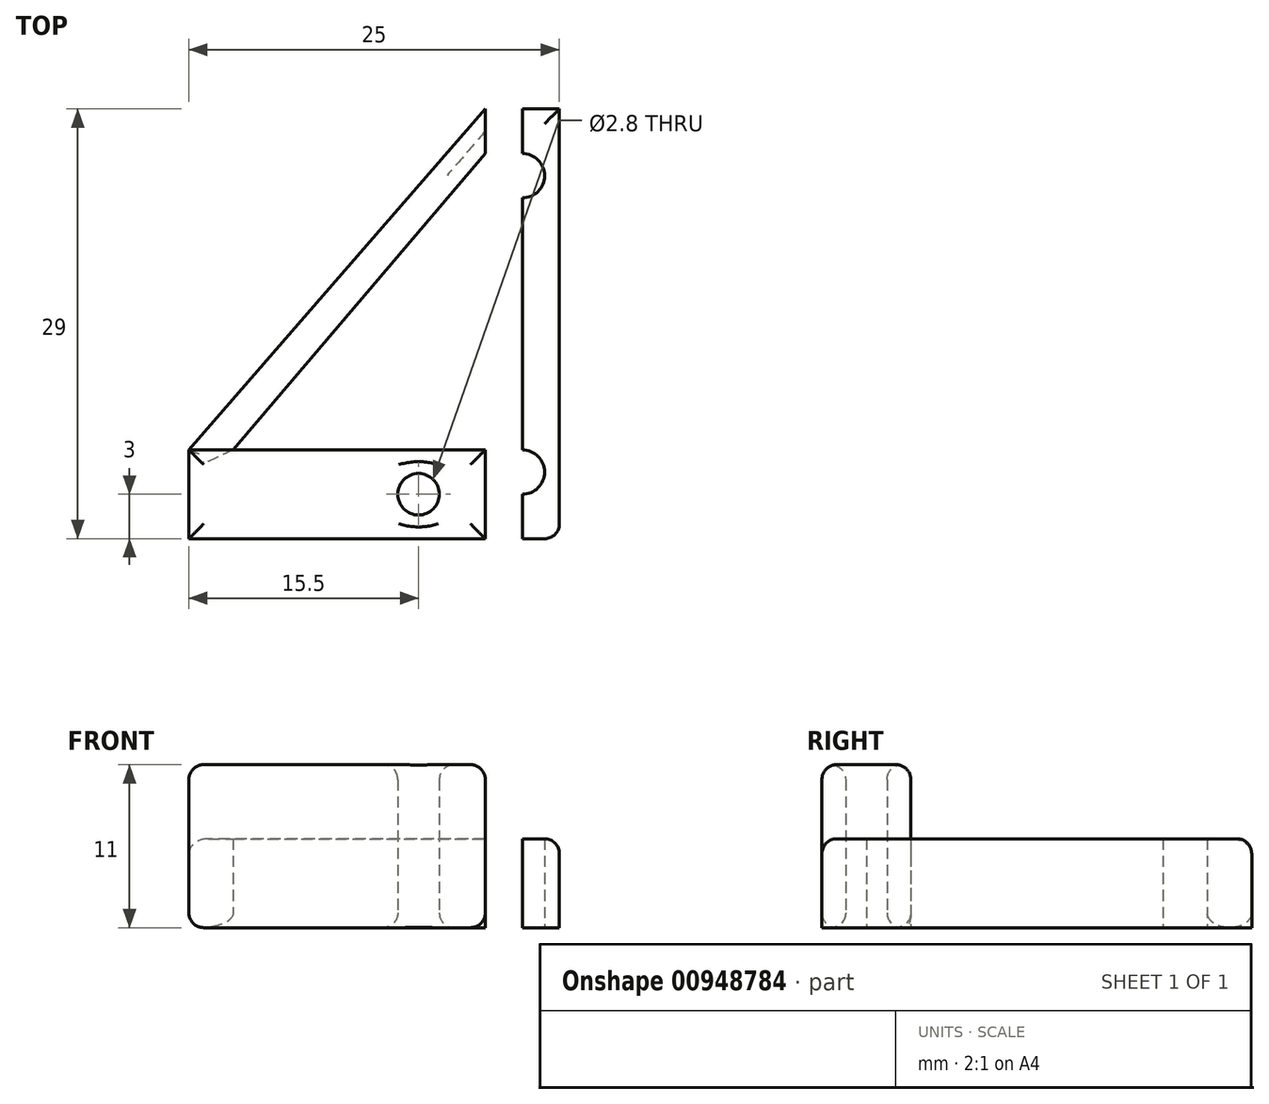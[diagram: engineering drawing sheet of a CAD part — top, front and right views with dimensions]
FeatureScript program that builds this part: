
annotation { "Feature Type Name" : "Feature", "Feature Type Description" : "" }
export const myFeature = defineFeature(function(context is Context, id is Id, definition is map)
    precondition{}
    {
        {
            var Q0;
            Q0=qCreatedBy(makeId("Top.planeOp"),FACE);
            var sketch = newSketch(context, id + "F0", { "sketchPlane" : qUnion([Q0])});
            skLineSegment(sketch, "E0.bottom", {"start": v(0, 0) * mm, "end": v(-20, 0) * mm});
            skLineSegment(sketch, "E0.top", {"start": v(0, 6) * mm, "end": v(-20, 6) * mm});
            skLineSegment(sketch, "E0.left", {"start": v(0, 0) * mm, "end": v(0, 6) * mm});
            skLineSegment(sketch, "E0.right", {"start": v(-20, 0) * mm, "end": v(-20, 6) * mm});
            skLineSegment(sketch, "E1", {"start": v(-20, 3) * mm, "end": v(0, 3) * mm});
            skCircle(sketch, "E2", {"center": v(-15.5, 3) * mm, "radius": 1.4 * mm});
            skCircle(sketch, "E3", {"center": v(-4.5, 3) * mm, "radius": 1.4 * mm});
            skPoint(sketch, "E4", {"position": v(-15.5, 4.4) * mm});
            skPoint(sketch, "E5", {"position": v(-4.5, 4.4) * mm});
            skPoint(sketch, "E6", {"position": v(-4.5, 1.6) * mm});
            skPoint(sketch, "E7", {"position": v(-15.5, 1.6) * mm});
            skLineSegment(sketch, "E8", {"start": v(-15.5, 4.4) * mm, "end": v(-4.5, 4.4) * mm});
            skLineSegment(sketch, "E9", {"start": v(-4.5, 1.6) * mm, "end": v(-15.5, 1.6) * mm});
            skLineSegment(sketch, "E10.bottom", {"start": v(0, 0) * mm, "end": v(5, 0) * mm});
            skLineSegment(sketch, "E10.top", {"start": v(0, 29) * mm, "end": v(5, 29) * mm});
            skLineSegment(sketch, "E10.left", {"start": v(0, 0) * mm, "end": v(0, 29) * mm});
            skLineSegment(sketch, "E10.right", {"start": v(5, 0) * mm, "end": v(5, 29) * mm});
            skPoint(sketch, "E11", {"position": v(5, 15) * mm});
            skLineSegment(sketch, "E12", {"start": v(5, 15) * mm, "end": v(5, 29) * mm});
            skLineSegment(sketch, "E13", {"start": v(2.5, 29) * mm, "end": v(2.5, 0) * mm});
            skCircle(sketch, "E14", {"center": v(2.5, 24.5) * mm, "radius": 1.5 * mm});
            skCircle(sketch, "E15", {"center": v(2.5, 4.5) * mm, "radius": 1.5 * mm});
            skPoint(sketch, "E16", {"position": v(0, 26) * mm});
            skPoint(sketch, "E17", {"position": v(-17, 6) * mm});
            skLineSegment(sketch, "E18", {"start": v(0, 29) * mm, "end": v(-20, 6) * mm});
            skLineSegment(sketch, "E19", {"start": v(-17, 6) * mm, "end": v(0, 26) * mm});
            skLineSegment(sketch, "E20.bottom", {"start": v(-11.5, 4.4) * mm, "end": v(-8.5, 4.4) * mm});
            skLineSegment(sketch, "E20.top", {"start": v(-11.5, 1.6) * mm, "end": v(-8.5, 1.6) * mm});
            skLineSegment(sketch, "E20.left", {"start": v(-11.5, 4.4) * mm, "end": v(-11.5, 1.6) * mm});
            skLineSegment(sketch, "E20.right", {"start": v(-8.5, 4.4) * mm, "end": v(-8.5, 1.6) * mm});
            skLineSegment(sketch, "E21", {"start": v(-10, 4.4) * mm, "end": v(-10, 1.6) * mm});
            skSolve(sketch);
        }
        {
            var Q0;
            {var subQ0=sQuery(id+"F0.wireOp",EDGE,"E18");Q0=makeQuery(id+"F0.imprint","IMPRINT",FACE,{"disambiguationData":[TD([[makeQuery(id+"F0.imprint","IMPRINT",EDGE,{"derivedFrom":subQ0}),1.0]])]});}
            var Q1;
            {var subQ11=sQuery(id+"F0.wireOp",EDGE,"E10.left");var subQ14=makeQuery(id+"F0.imprint","INTERSECT",VERTEX,{"derivedFrom":[sQuery(id+"F0.wireOp",EDGE,"E0.top"),subQ11]});Q1=makeQuery(id+"F0.imprint","IMPRINT",FACE,{"disambiguationData":[TD([[makeQuery(id+"F0.imprint","IMPRINT",EDGE,{"disambiguationData":[TD([[subQ14,1.0]])],"derivedFrom":subQ11}),-1.0]])]});}
            var Q2;
            {var subQ1=sQuery(id+"F0.wireOp",EDGE,"E10.right");Q2=makeQuery(id+"F0.imprint","IMPRINT",FACE,{"disambiguationData":[TD([[makeQuery(id+"F0.imprint","IMPRINT",EDGE,{"derivedFrom":subQ1}),1.0]])]});}
            var Q3;
            {var subQ13=sQuery(id+"F0.wireOp",EDGE,"E8");Q3=makeQuery(id+"F0.imprint","IMPRINT",FACE,{"disambiguationData":[TD([[makeQuery(id+"F0.imprint","IMPRINT",EDGE,{"derivedFrom":subQ13}),1.0]])]});}
            var Q4;
            {var subQ6=sQuery(id+"F0.wireOp",EDGE,"E0.bottom");Q4=makeQuery(id+"F0.imprint","IMPRINT",FACE,{"disambiguationData":[TD([[makeQuery(id+"F0.imprint","IMPRINT",EDGE,{"derivedFrom":subQ6}),-1.0]])]});}
            extrude(context, id + "F1", {"entities" : qUnion([Q0, Q1, Q2, Q3, Q4]), "depth" : 6 * mm, "offsetDistance" : 25 * mm});
        }
        {
            var Q0;
            {var subQ0=sQuery(id+"F0.wireOp",EDGE,"E2");var subQ1=sQuery(id+"F0.wireOp",EDGE,"E1");var subQ2=makeQuery(id+"F0.imprint","INTERSECT",VERTEX,{"disambiguationData":[OD(0.0)],"derivedFrom":[subQ1,subQ0]});Q0=makeQuery(id+"F0.imprint","IMPRINT",FACE,{"disambiguationData":[TD([[makeQuery(id+"F0.imprint","IMPRINT",EDGE,{"disambiguationData":[TD([[subQ2,-1.0]])],"derivedFrom":subQ1}),-1.0]])]});}
            var Q1;
            {var subQ5=sQuery(id+"F0.wireOp",EDGE,"E9");Q1=makeQuery(id+"F0.imprint","IMPRINT",FACE,{"disambiguationData":[TD([[makeQuery(id+"F0.imprint","IMPRINT",EDGE,{"derivedFrom":subQ5}),-1.0]])]});}
            var Q2;
            {var subQ5=sQuery(id+"F0.wireOp",EDGE,"E8");Q2=makeQuery(id+"F0.imprint","IMPRINT",FACE,{"disambiguationData":[TD([[makeQuery(id+"F0.imprint","IMPRINT",EDGE,{"derivedFrom":subQ5}),-1.0]])]});}
            var Q3;
            {var subQ0=sQuery(id+"F0.wireOp",EDGE,"E3");var subQ1=sQuery(id+"F0.wireOp",EDGE,"E1");var subQ2=makeQuery(id+"F0.imprint","INTERSECT",VERTEX,{"disambiguationData":[OD(0.0)],"derivedFrom":[subQ1,subQ0]});Q3=makeQuery(id+"F0.imprint","IMPRINT",FACE,{"disambiguationData":[TD([[makeQuery(id+"F0.imprint","IMPRINT",EDGE,{"disambiguationData":[TD([[subQ2,-1.0]])],"derivedFrom":subQ1}),1.0]])]});}
            var Q4;
            {var subQ0=sQuery(id+"F0.wireOp",EDGE,"E3");var subQ1=sQuery(id+"F0.wireOp",EDGE,"E1");var subQ2=makeQuery(id+"F0.imprint","INTERSECT",VERTEX,{"disambiguationData":[OD(0.0)],"derivedFrom":[subQ1,subQ0]});Q4=makeQuery(id+"F0.imprint","IMPRINT",FACE,{"disambiguationData":[TD([[makeQuery(id+"F0.imprint","IMPRINT",EDGE,{"disambiguationData":[TD([[subQ2,-1.0]])],"derivedFrom":subQ1}),-1.0]])]});}
            var Q5;
            {var subQ0=sQuery(id+"F0.wireOp",EDGE,"E2");var subQ1=sQuery(id+"F0.wireOp",EDGE,"E1");var subQ2=makeQuery(id+"F0.imprint","INTERSECT",VERTEX,{"disambiguationData":[OD(0.0)],"derivedFrom":[subQ1,subQ0]});Q5=makeQuery(id+"F0.imprint","IMPRINT",FACE,{"disambiguationData":[TD([[makeQuery(id+"F0.imprint","IMPRINT",EDGE,{"disambiguationData":[TD([[subQ2,-1.0]])],"derivedFrom":subQ1}),1.0]])]});}
            extrude(context, id + "F2", {"entities" : qUnion([Q0, Q1, Q2, Q3, Q4, Q5]), "operationType" : NewBodyOperationType.ADD, "depth" : 11 * mm, "offsetDistance" : 25 * mm});
        }
        {
            var Q0;
            Q0=makeQuery(id+"F2.opExtrude","CAP_FACE",FACE,{"disambiguationData":[OSD([sQuery(id+"F0.wireOp",EDGE,"E2"),sQuery(id+"F0.wireOp",EDGE,"E3"),sQuery(id+"F0.wireOp",EDGE,"E8"),sQuery(id+"F0.wireOp",EDGE,"E9")])],"isStart":false});
            fillet(context, id + "F3", {"entities" : qUnion([Q0]), "radius" : 1 * mm, "tangentPropagation" : true, "allowEdgeOverflow" : false});
        }
        {
            var Q0;
            {var subQ0=sQuery(id+"F0.wireOp",EDGE,"E9");var subQ1=sQuery(id+"F0.wireOp",EDGE,"E8");var subQ2=sQuery(id+"F0.wireOp",EDGE,"E3");var subQ3=sQuery(id+"F0.wireOp",EDGE,"E2");Q0=makeQuery(id+"F2.boolean.opBoolean","MERGE",FACE,{"derivedFrom":[makeQuery(id+"F1.opExtrude","CAP_FACE",FACE,{"disambiguationData":[OSD([sQuery(id+"F0.wireOp",EDGE,"E0.bottom"),sQuery(id+"F0.wireOp",EDGE,"E0.top"),sQuery(id+"F0.wireOp",EDGE,"E0.right"),subQ3,subQ2,subQ1,subQ0,sQuery(id+"F0.wireOp",EDGE,"E10.bottom"),sQuery(id+"F0.wireOp",EDGE,"E10.top"),sQuery(id+"F0.wireOp",EDGE,"E10.left"),sQuery(id+"F0.wireOp",EDGE,"E10.right"),sQuery(id+"F0.wireOp",EDGE,"E12"),sQuery(id+"F0.wireOp",EDGE,"E14"),sQuery(id+"F0.wireOp",EDGE,"E15"),sQuery(id+"F0.wireOp",EDGE,"E18"),sQuery(id+"F0.wireOp",EDGE,"E19")])],"isStart":true}),makeQuery(id+"F2.opExtrude","CAP_FACE",FACE,{"disambiguationData":[OSD([subQ3,subQ2,subQ1,subQ0])],"isStart":true})]});}
            var Q1;
            Q1=makeQuery(id+"F1.opExtrude","CAP_EDGE",EDGE,{"disambiguationData":[OSD([sQuery(id+"F0.wireOp",EDGE,"E10.right"),sQuery(id+"F0.wireOp",EDGE,"E12")])],"isStart":false});
            var Q2;
            Q2=makeQuery(id+"F1.opExtrude","SWEPT_EDGE",EDGE,{"disambiguationData":[OSD([sQuery(id+"F0.wireOp",EDGE,"E10.bottom"),sQuery(id+"F0.wireOp",EDGE,"E10.right")])]});
            var Q3;
            Q3=makeQuery(id+"F1.opExtrude","CAP_EDGE",EDGE,{"disambiguationData":[OSD([sQuery(id+"F0.wireOp",EDGE,"E18")])],"isStart":false});
            var Q4;
            Q4=makeQuery(id+"F1.opExtrude","CAP_EDGE",EDGE,{"disambiguationData":[OSD([sQuery(id+"F0.wireOp",EDGE,"E0.right")])],"isStart":false});
            var Q5;
            Q5=makeQuery(id+"F1.opExtrude","CAP_EDGE",EDGE,{"disambiguationData":[OSD([sQuery(id+"F0.wireOp",EDGE,"E10.top")])],"isStart":false});
            var Q6;
            Q6=makeQuery(id+"F1.opExtrude","CAP_EDGE",EDGE,{"disambiguationData":[OSD([sQuery(id+"F0.wireOp",EDGE,"E0.bottom"),sQuery(id+"F0.wireOp",EDGE,"E10.bottom")])],"isStart":false});
            fillet(context, id + "F4", {"entities" : qUnion([Q0, Q1, Q2, Q3, Q4, Q5, Q6]), "radius" : 1 * mm, "tangentPropagation" : true, "allowEdgeOverflow" : false});
        }
    });
